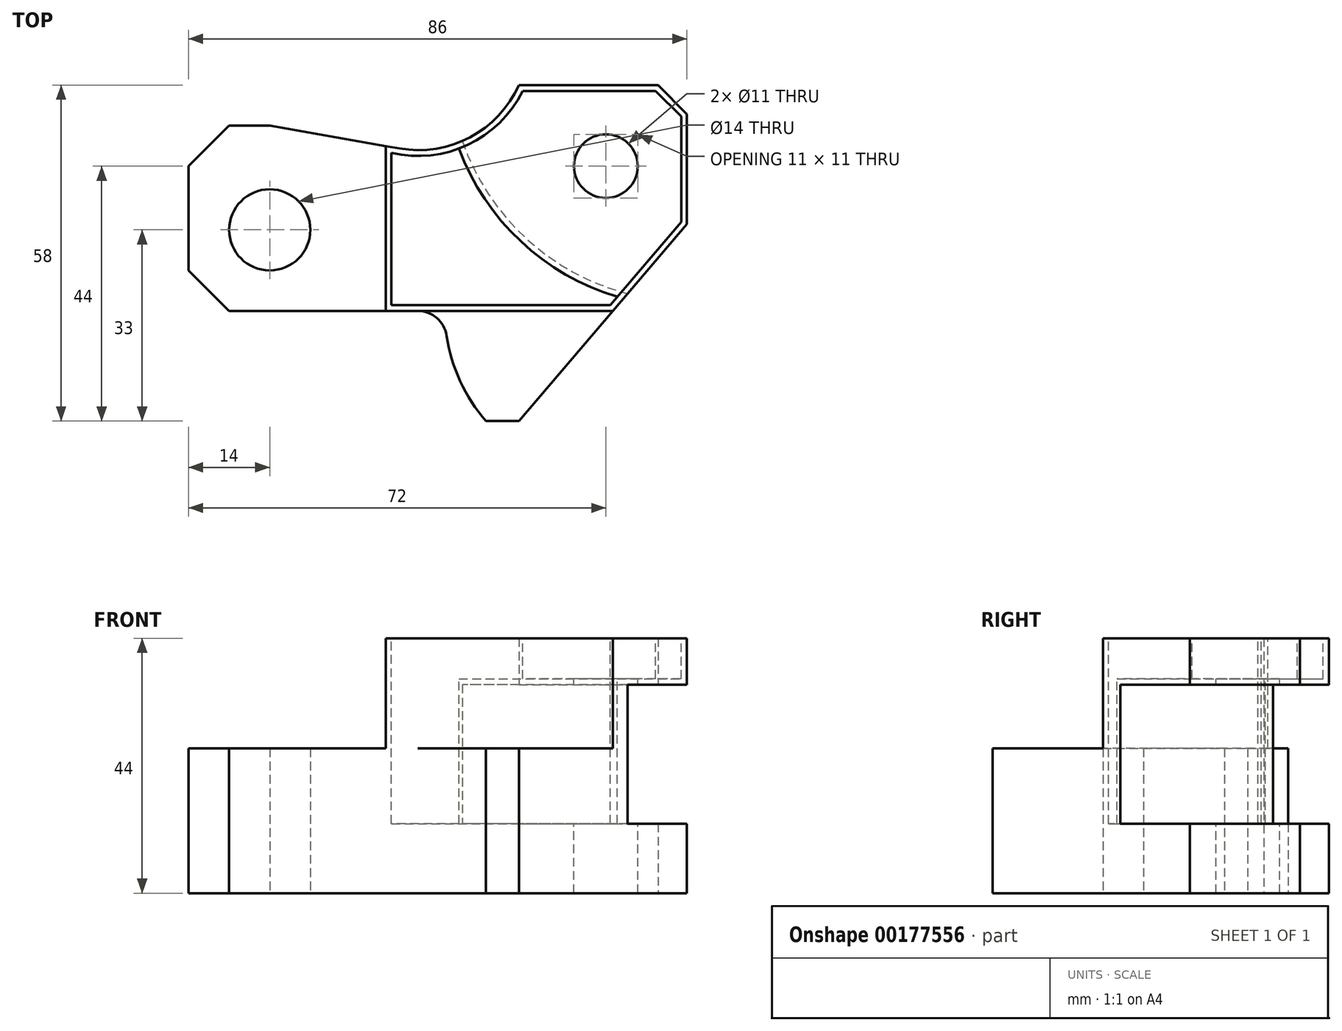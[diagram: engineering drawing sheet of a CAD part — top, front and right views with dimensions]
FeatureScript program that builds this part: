
annotation { "Feature Type Name" : "Feature", "Feature Type Description" : "" }
export const myFeature = defineFeature(function(context is Context, id is Id, definition is map)
    precondition{}
    {
        {
            assignVariable(context, id + "F0", {"name" : "C", "anyValue" : 44});
        }
        {
            var Q0;
            Q0=qCreatedBy(makeId("Top.planeOp"),FACE);
            var sketch = newSketch(context, id + "F1", { "sketchPlane" : qUnion([Q0])});
            skLineSegment(sketch, "E0", {"start": v(0, 0) * mm, "end": v(29, 34) * mm});
            skLineSegment(sketch, "E1", {"start": v(29, 34) * mm, "end": v(29, 53) * mm});
            skLineSegment(sketch, "E2", {"start": v(29, 53) * mm, "end": v(24, 58) * mm});
            skLineSegment(sketch, "E3", {"start": v(24, 58) * mm, "end": v(0, 58) * mm});
            skLineSegment(sketch, "E4", {"start": v(0, 0) * mm, "end": v(-5.7, 0) * mm});
            skArc(sketch, "E5", {"start": v(-12.48, 14.74) * mm, "mid": v(-10.14, 6.88) * mm, "end": v(-5.7, 0) * mm});
            skArc(sketch, "E6", {"start": v(-12.48, 14.74) * mm, "mid": v(-14.16, 17.79) * mm, "end": v(-17.42, 19) * mm});
            skLineSegment(sketch, "E7", {"start": v(-17.42, 19) * mm, "end": v(-50, 19) * mm});
            skLineSegment(sketch, "E8", {"start": v(-50, 19) * mm, "end": v(-57, 26) * mm});
            skLineSegment(sketch, "E9", {"start": v(-57, 26) * mm, "end": v(-57, 44) * mm});
            skLineSegment(sketch, "E10", {"start": v(-57, 44) * mm, "end": v(-50, 51) * mm});
            skLineSegment(sketch, "E11", {"start": v(-50, 51) * mm, "end": v(-43, 51) * mm});
            skLineSegment(sketch, "E12", {"start": v(-43, 51) * mm, "end": v(-20.64, 47.06) * mm});
            skArc(sketch, "E13", {"start": v(-20.64, 47.06) * mm, "mid": v(-8.44, 48.98) * mm, "end": v(0, 58) * mm});
            skCircle(sketch, "E14", {"center": v(-43, 33) * mm, "radius": 7 * mm});
            skSolve(sketch);
        }
        {
            var Q0;
            Q0 = qSketchRegion(id + "F1", true);
            extrude(context, id + "F2", {"entities" : qUnion([Q0]), "endBound" : BoundingType.SYMMETRIC, "depth" : (getVariable(context, 'C')) * mm});
        }
        {
            var Q0;
            Q0=makeQuery(id+"F2.opExtrude","CAP_FACE",FACE,{"disambiguationData":[OSD([sQuery(id+"F1.wireOp",EDGE,"E0"),sQuery(id+"F1.wireOp",EDGE,"E1"),sQuery(id+"F1.wireOp",EDGE,"E2"),sQuery(id+"F1.wireOp",EDGE,"E3"),sQuery(id+"F1.wireOp",EDGE,"E4"),sQuery(id+"F1.wireOp",EDGE,"E5"),sQuery(id+"F1.wireOp",EDGE,"E6"),sQuery(id+"F1.wireOp",EDGE,"E7"),sQuery(id+"F1.wireOp",EDGE,"E8"),sQuery(id+"F1.wireOp",EDGE,"E9"),sQuery(id+"F1.wireOp",EDGE,"E10"),sQuery(id+"F1.wireOp",EDGE,"E11"),sQuery(id+"F1.wireOp",EDGE,"E12"),sQuery(id+"F1.wireOp",EDGE,"E13"),sQuery(id+"F1.wireOp",EDGE,"E14")])],"isStart":false});
            var sketch = newSketch(context, id + "F3", { "sketchPlane" : qUnion([Q0])});
            skCircle(sketch, "E15", {"center": v(15, 44) * mm, "radius": 5.5 * mm});
            skSolve(sketch);
        }
        {
            var Q0;
            Q0 = qSketchRegion(id + "F3", true);
            extrude(context, id + "F4", {"entities" : qUnion([Q0]), "operationType" : NewBodyOperationType.REMOVE, "endBound" : BoundingType.THROUGH_ALL, "oppositeDirection" : true, "depth" : 25 * mm});
        }
        {
            var Q0;
            Q0=makeQuery(id+"F2.opExtrude","CAP_FACE",FACE,{"disambiguationData":[OSD([sQuery(id+"F1.wireOp",EDGE,"E0"),sQuery(id+"F1.wireOp",EDGE,"E1"),sQuery(id+"F1.wireOp",EDGE,"E2"),sQuery(id+"F1.wireOp",EDGE,"E3"),sQuery(id+"F1.wireOp",EDGE,"E4"),sQuery(id+"F1.wireOp",EDGE,"E5"),sQuery(id+"F1.wireOp",EDGE,"E6"),sQuery(id+"F1.wireOp",EDGE,"E7"),sQuery(id+"F1.wireOp",EDGE,"E8"),sQuery(id+"F1.wireOp",EDGE,"E9"),sQuery(id+"F1.wireOp",EDGE,"E10"),sQuery(id+"F1.wireOp",EDGE,"E11"),sQuery(id+"F1.wireOp",EDGE,"E12"),sQuery(id+"F1.wireOp",EDGE,"E13"),sQuery(id+"F1.wireOp",EDGE,"E14")])],"isStart":false});
            var sketch = newSketch(context, id + "F5", { "sketchPlane" : qUnion([Q0])});
            skLineSegment(sketch, "E16", {"start": v(-23, 47.47) * mm, "end": v(-23, 19) * mm});
            skLineSegment(sketch, "E17", {"start": v(-23, 19) * mm, "end": v(16.2, 19) * mm});
            skLineSegment(sketch, "E18.0.0", {"start": v(-5.7, 0) * mm, "end": v(0, 0) * mm});
            skLineSegment(sketch, "E18.0.1", {"start": v(0, 0) * mm, "end": v(16.2, 19) * mm});
            skLineSegment(sketch, "E18.0.6", {"start": v(-23, 47.47) * mm, "end": v(-43, 51) * mm});
            skLineSegment(sketch, "E18.0.7", {"start": v(-43, 51) * mm, "end": v(-50, 51) * mm});
            skLineSegment(sketch, "E18.0.8", {"start": v(-50, 51) * mm, "end": v(-57, 44) * mm});
            skLineSegment(sketch, "E18.0.9", {"start": v(-57, 44) * mm, "end": v(-57, 26) * mm});
            skLineSegment(sketch, "E18.0.10", {"start": v(-57, 26) * mm, "end": v(-50, 19) * mm});
            skLineSegment(sketch, "E18.0.11", {"start": v(-50, 19) * mm, "end": v(-17.42, 19) * mm});
            skArc(sketch, "E18.0.12", {"start": v(-17.42, 19) * mm, "mid": v(-14.16, 17.79) * mm, "end": v(-12.48, 14.74) * mm});
            skArc(sketch, "E18.0.13", {"start": v(-12.48, 14.74) * mm, "mid": v(-10.14, 6.88) * mm, "end": v(-5.7, 0) * mm});
            skSolve(sketch);
        }
        {
            var Q0;
            Q0 = qSketchRegion(id + "F5", true);
            extrude(context, id + "F6", {"entities" : qUnion([Q0]), "operationType" : NewBodyOperationType.REMOVE, "oppositeDirection" : true, "depth" : 19 * mm});
        }
        {
            var Q0;
            Q0=makeQuery(id+"F2.opExtrude","CAP_FACE",FACE,{"disambiguationData":[OSD([sQuery(id+"F1.wireOp",EDGE,"E0"),sQuery(id+"F1.wireOp",EDGE,"E1"),sQuery(id+"F1.wireOp",EDGE,"E2"),sQuery(id+"F1.wireOp",EDGE,"E3"),sQuery(id+"F1.wireOp",EDGE,"E4"),sQuery(id+"F1.wireOp",EDGE,"E5"),sQuery(id+"F1.wireOp",EDGE,"E6"),sQuery(id+"F1.wireOp",EDGE,"E7"),sQuery(id+"F1.wireOp",EDGE,"E8"),sQuery(id+"F1.wireOp",EDGE,"E9"),sQuery(id+"F1.wireOp",EDGE,"E10"),sQuery(id+"F1.wireOp",EDGE,"E11"),sQuery(id+"F1.wireOp",EDGE,"E12"),sQuery(id+"F1.wireOp",EDGE,"E13"),sQuery(id+"F1.wireOp",EDGE,"E14")])],"isStart":true});
            cPlane(context, id + "F7", {"entities" : qUnion([Q0]), "cplaneType" : CPlaneType.OFFSET, "offset" : 12 * mm, "oppositeDirection" : true, "width" : 150 * mm, "height" : 150 * mm});
        }
        {
            var Q0;
            Q0=qCreatedBy(id+"F7.planeOp",FACE);
            var sketch = newSketch(context, id + "F8", { "sketchPlane" : qUnion([Q0])});
            skCircle(sketch, "E19", {"center": v(29, -61.7) * mm, "radius": 41 * mm});
            skLineSegment(sketch, "E20.0", {"start": v(16.2, -19) * mm, "end": v(29, -34) * mm, "construction": true});
            skPoint(sketch, "E21", {"position": v(18.76, -22) * mm});
            skSolve(sketch);
        }
        {
            var Q0;
            Q0 = qSketchRegion(id + "F8", true);
            extrude(context, id + "F9", {"entities" : qUnion([Q0]), "operationType" : NewBodyOperationType.REMOVE, "oppositeDirection" : true, "depth" : 24 * mm});
        }
        {
            var Q0;
            Q0=makeQuery(id+"F2.opExtrude","CAP_FACE",FACE,{"disambiguationData":[OSD([sQuery(id+"F1.wireOp",EDGE,"E0"),sQuery(id+"F1.wireOp",EDGE,"E1"),sQuery(id+"F1.wireOp",EDGE,"E2"),sQuery(id+"F1.wireOp",EDGE,"E3"),sQuery(id+"F1.wireOp",EDGE,"E4"),sQuery(id+"F1.wireOp",EDGE,"E5"),sQuery(id+"F1.wireOp",EDGE,"E6"),sQuery(id+"F1.wireOp",EDGE,"E7"),sQuery(id+"F1.wireOp",EDGE,"E8"),sQuery(id+"F1.wireOp",EDGE,"E9"),sQuery(id+"F1.wireOp",EDGE,"E10"),sQuery(id+"F1.wireOp",EDGE,"E11"),sQuery(id+"F1.wireOp",EDGE,"E12"),sQuery(id+"F1.wireOp",EDGE,"E13"),sQuery(id+"F1.wireOp",EDGE,"E14")])],"isStart":false});
            var sketch = newSketch(context, id + "F10", { "sketchPlane" : qUnion([Q0])});
            skLineSegment(sketch, "E22.0.0", {"start": v(-20.64, 47.06) * mm, "end": v(-23, 47.47) * mm, "construction": true});
            skLineSegment(sketch, "E22.0.1", {"start": v(-23, 47.47) * mm, "end": v(-23, 19) * mm, "construction": true});
            skLineSegment(sketch, "E22.0.2", {"start": v(-23, 19) * mm, "end": v(16.2, 19) * mm, "construction": true});
            skLineSegment(sketch, "E22.0.3", {"start": v(16.2, 19) * mm, "end": v(29, 34) * mm, "construction": true});
            skLineSegment(sketch, "E22.0.4", {"start": v(29, 34) * mm, "end": v(29, 53) * mm, "construction": true});
            skLineSegment(sketch, "E22.0.5", {"start": v(29, 53) * mm, "end": v(24, 58) * mm, "construction": true});
            skLineSegment(sketch, "E22.0.6", {"start": v(24, 58) * mm, "end": v(0, 58) * mm, "construction": true});
            skArc(sketch, "E22.0.7", {"start": v(0, 58) * mm, "mid": v(-8.44, 48.98) * mm, "end": v(-20.64, 47.06) * mm, "construction": true});
            skLineSegment(sketch, "E23.0", {"start": v(28, 52.59) * mm, "end": v(23.59, 57) * mm});
            skLineSegment(sketch, "E23.1", {"start": v(28, 34.37) * mm, "end": v(28, 52.59) * mm});
            skArc(sketch, "E23.2", {"start": v(0.64, 57) * mm, "mid": v(-8.8, 47.68) * mm, "end": v(-22, 46.32) * mm});
            skLineSegment(sketch, "E23.3", {"start": v(-22, 46.32) * mm, "end": v(-22, 20) * mm});
            skLineSegment(sketch, "E23.4", {"start": v(-22, 20) * mm, "end": v(15.74, 20) * mm});
            skLineSegment(sketch, "E23.5", {"start": v(23.59, 57) * mm, "end": v(0.64, 57) * mm});
            skLineSegment(sketch, "E23.6", {"start": v(15.74, 20) * mm, "end": v(28, 34.37) * mm});
            skSolve(sketch);
        }
        {
            var Q0;
            Q0 = qSketchRegion(id + "F10", true);
            var Q1;
            Q1=makeQuery(id+"F9.boolean.opBoolean","COPY",FACE,{"derivedFrom":makeQuery(id+"F9.opExtrude","CAP_FACE",FACE,{"disambiguationData":[OSD([sQuery(id+"F8.wireOp",EDGE,"E19")])],"isStart":false})});
            extrude(context, id + "F11", {"entities" : qUnion([Q0]), "operationType" : NewBodyOperationType.REMOVE, "oppositeDirection" : true, "endBoundEntityFace" : qUnion([Q1]), "depth" : (getVariable(context, 'C') - 12 - 24 - 1) * mm});
        }
        {
            var Q0;
            Q0=makeQuery(id+"F11.boolean.opBoolean","COPY",FACE,{"derivedFrom":makeQuery(id+"F11.opExtrude","CAP_FACE",FACE,{"disambiguationData":[OSD([sQuery(id+"F10.wireOp",EDGE,"E23.0"),sQuery(id+"F10.wireOp",EDGE,"E23.1"),sQuery(id+"F10.wireOp",EDGE,"E23.2"),sQuery(id+"F10.wireOp",EDGE,"E23.3"),sQuery(id+"F10.wireOp",EDGE,"E23.4"),sQuery(id+"F10.wireOp",EDGE,"E23.5"),sQuery(id+"F10.wireOp",EDGE,"E23.6")])],"isStart":false})});
            var sketch = newSketch(context, id + "F12", { "sketchPlane" : qUnion([Q0])});
            skArc(sketch, "E24.0", {"start": v(17.7, 22.3) * mm, "mid": v(1.15, 31.62) * mm, "end": v(-9.43, 47.4) * mm, "construction": true});
            skLineSegment(sketch, "E25.0", {"start": v(-22, 46.32) * mm, "end": v(-22, 20) * mm});
            skArc(sketch, "E26.0", {"start": v(-10.35, 47.03) * mm, "mid": v(-16.12, 45.8) * mm, "end": v(-22, 46.32) * mm});
            skLineSegment(sketch, "E27.0", {"start": v(-22, 20) * mm, "end": v(15.74, 20) * mm});
            skLineSegment(sketch, "E28.0", {"start": v(15.74, 20) * mm, "end": v(16.99, 21.46) * mm});
            skArc(sketch, "E29.0", {"start": v(16.99, 21.46) * mm, "mid": v(0.31, 31.03) * mm, "end": v(-10.35, 47.03) * mm});
            skSolve(sketch);
        }
        {
            var Q0;
            Q0 = qSketchRegion(id + "F12", true);
            var Q1;
            Q1=makeQuery(id+"F9.boolean.opBoolean","COPY",FACE,{"derivedFrom":makeQuery(id+"F9.opExtrude","CAP_FACE",FACE,{"disambiguationData":[OSD([sQuery(id+"F8.wireOp",EDGE,"E19")])],"isStart":true})});
            extrude(context, id + "F13", {"entities" : qUnion([Q0]), "operationType" : NewBodyOperationType.REMOVE, "endBound" : BoundingType.UP_TO_SURFACE, "oppositeDirection" : true, "endBoundEntityFace" : qUnion([Q1]), "depth" : 25 * mm});
        }
    });
